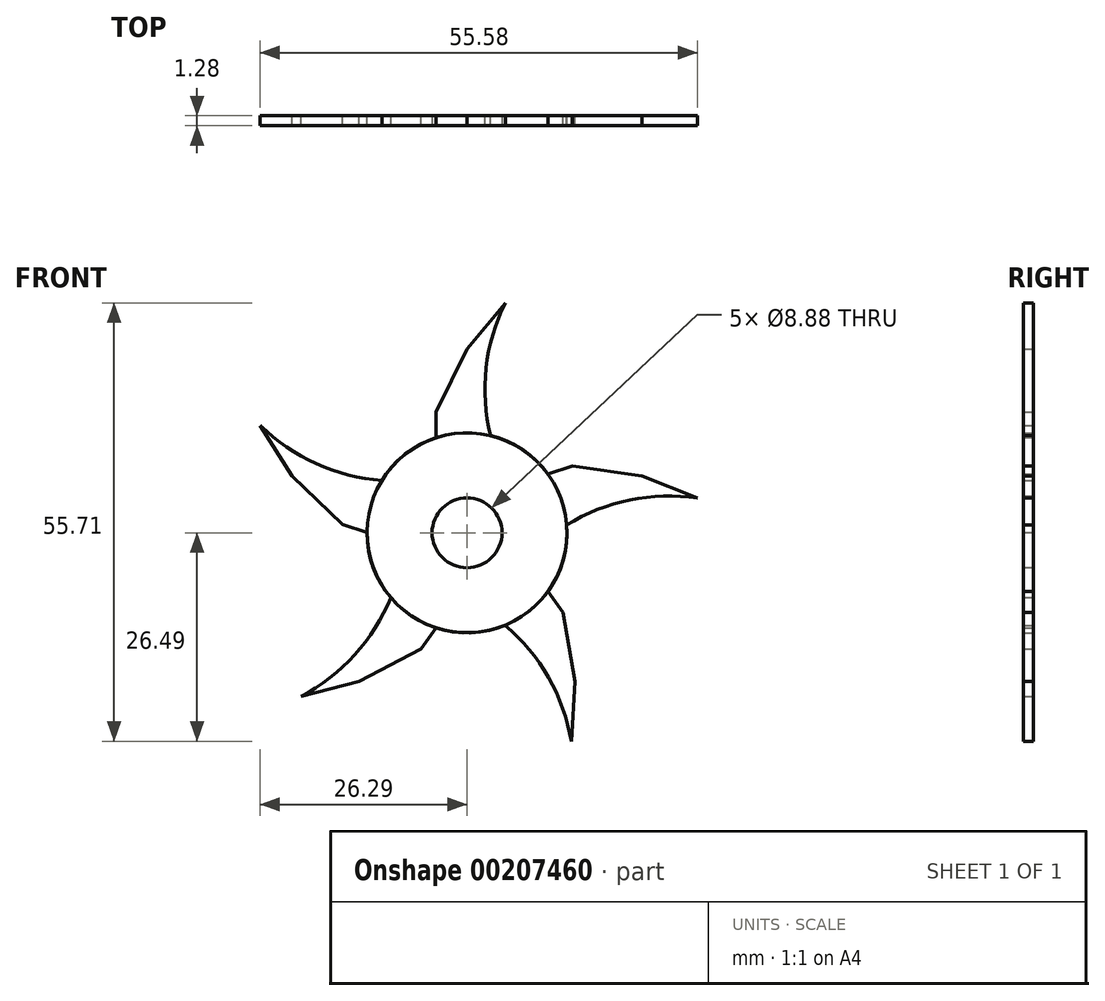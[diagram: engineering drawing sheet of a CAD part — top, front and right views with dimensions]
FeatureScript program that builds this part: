
annotation { "Feature Type Name" : "Feature", "Feature Type Description" : "" }
export const myFeature = defineFeature(function(context is Context, id is Id, definition is map)
    precondition{}
    {
        {
            var Q0;
            Q0=qCreatedBy(makeId("Front.planeOp"),FACE);
            var sketch = newSketch(context, id + "F0", { "sketchPlane" : qUnion([Q0])});
            skCircle(sketch, "E0", {"center": v(0, 0) * mm, "radius": 12.7 * mm});
            skSolve(sketch);
        }
        {
            var Q0;
            Q0=qSketchRegion(id+"F0",true);
            extrude(context, id + "F1", {"entities" : qUnion([Q0]), "endBound" : BoundingType.SYMMETRIC, "depth" : 1.27 * mm});
        }
        {
            var Q0;
            Q0=qCreatedBy(makeId("Front.planeOp"),FACE);
            var sketch = newSketch(context, id + "F2", { "sketchPlane" : qUnion([Q0])});
            skLineSegment(sketch, "E1.top", {"start": v(3.9, 9.4) * mm, "end": v(-3.9, 9.4) * mm});
            skLineSegment(sketch, "E1.right", {"start": v(-3.9, 15.36) * mm, "end": v(-3.9, 9.4) * mm});
            skPoint(sketch, "E1.middle", {"position": v(0, 12.38) * mm});
            skLineSegment(sketch, "E2", {"start": v(-3.9, 15.36) * mm, "end": v(0, 23.36) * mm});
            skLineSegment(sketch, "E3", {"start": v(0, 23.36) * mm, "end": v(4.86, 29.22) * mm});
            skArc(sketch, "E4", {"start": v(4.86, 29.22) * mm, "mid": v(2.3, 19.4) * mm, "end": v(3.9, 9.4) * mm});
            skSolve(sketch);
        }
        {
            var Q0;
            Q0=qSketchRegion(id+"F2",true);
            extrude(context, id + "F3", {"entities" : qUnion([Q0]), "operationType" : NewBodyOperationType.ADD, "endBound" : BoundingType.SYMMETRIC, "depth" : 1.27 * mm});
        }
        {
            var Q0;
            Q0=makeQuery(id+"F1.opExtrude","SWEPT_BODY",BODY,{"disambiguationData":[OSD([sQuery(id+"F0.wireOp",EDGE,"E0")])]});
            var Q1;
            Q1=sQuery(id+"F0.wireOp",EDGE,"E0");
            circularPattern(context, id + "F4", {"entities" : qUnion([Q0]), "axis" : qUnion([Q1]), "angle" : 360 * degree, "instanceCount" : 5, "equalSpace" : true});
        }
        {
            var Q0;
            Q0=qCreatedBy(makeId("Front.planeOp"),FACE);
            var sketch = newSketch(context, id + "F5", { "sketchPlane" : qUnion([Q0])});
            skCircle(sketch, "E5", {"center": v(0, 0) * mm, "radius": 4.44 * mm});
            skSolve(sketch);
        }
        {
            var Q0;
            Q0=qSketchRegion(id+"F5",true);
            extrude(context, id + "F6", {"entities" : qUnion([Q0]), "operationType" : NewBodyOperationType.REMOVE, "endBound" : BoundingType.SYMMETRIC, "oppositeDirection" : true, "depth" : 1.27 * mm});
        }
    });
